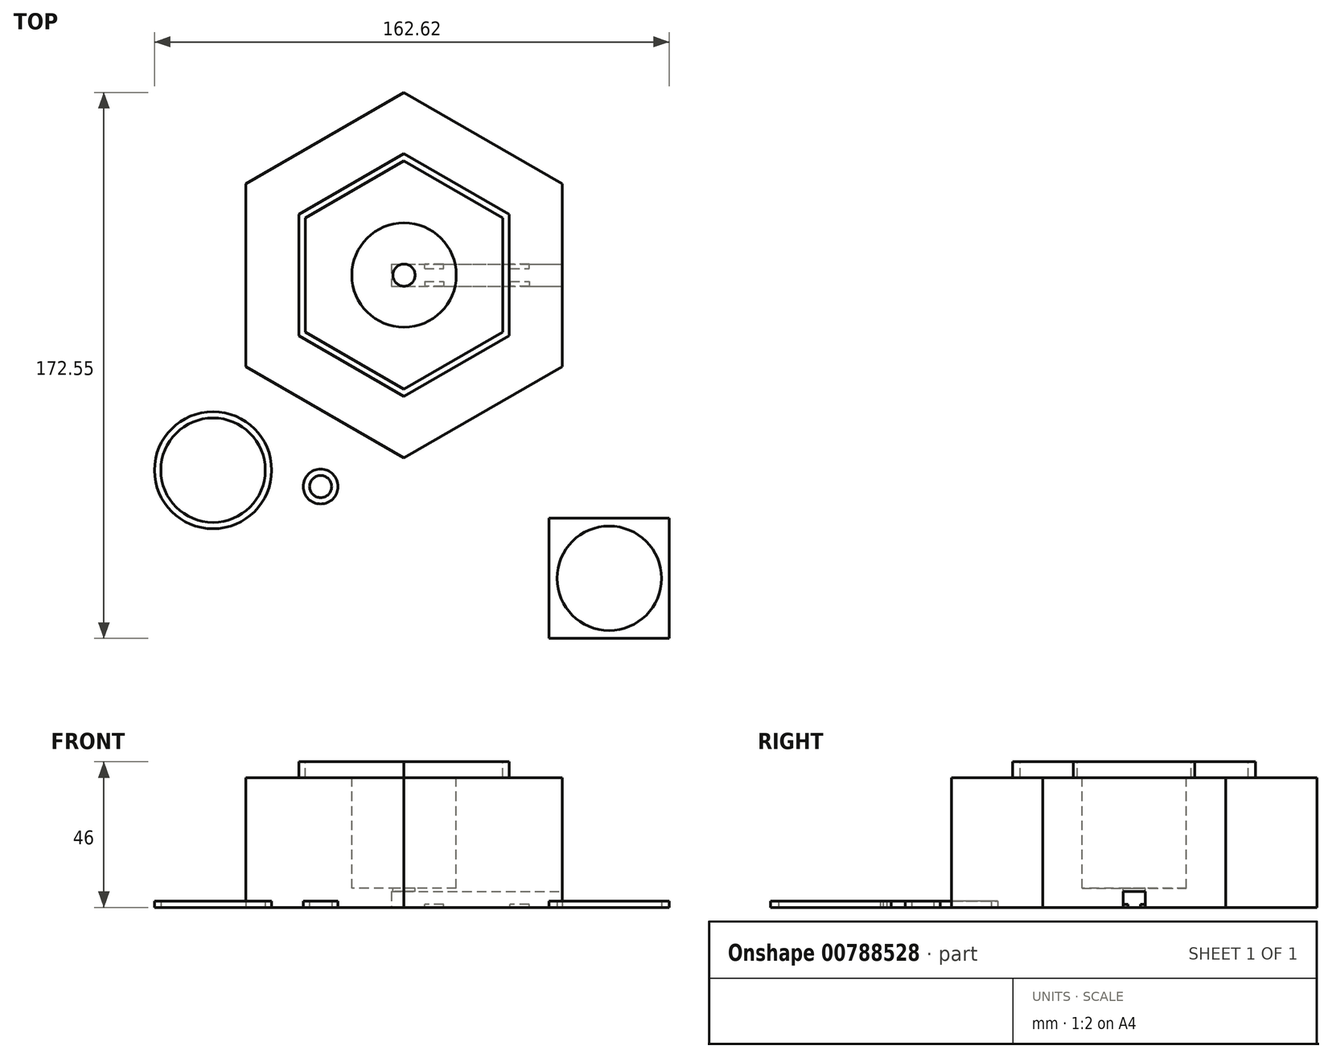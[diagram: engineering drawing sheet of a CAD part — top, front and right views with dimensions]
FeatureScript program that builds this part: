
annotation { "Feature Type Name" : "Feature", "Feature Type Description" : "" }
export const myFeature = defineFeature(function(context is Context, id is Id, definition is map)
    precondition{}
    {
        {
            var Q0;
            Q0=qCreatedBy(makeId("Top.planeOp"),FACE);
            var sketch = newSketch(context, id + "F0", { "sketchPlane" : qUnion([Q0])});
            skCircle(sketch, "E0.cCircle", {"center": v(0, 0) * mm, "radius": 50 * mm, "construction": true});
            skLineSegment(sketch, "E0.0", {"start": v(0, 57.73) * mm, "end": v(50, 28.87) * mm});
            skLineSegment(sketch, "E0.1", {"start": v(50, 28.87) * mm, "end": v(50, -28.87) * mm});
            skLineSegment(sketch, "E0.2", {"start": v(50, -28.87) * mm, "end": v(0, -57.73) * mm});
            skLineSegment(sketch, "E0.3", {"start": v(0, -57.73) * mm, "end": v(-50, -28.87) * mm});
            skLineSegment(sketch, "E0.4", {"start": v(-50, -28.87) * mm, "end": v(-50, 28.87) * mm});
            skLineSegment(sketch, "E0.5", {"start": v(-50, 28.87) * mm, "end": v(0, 57.73) * mm});
            skPoint(sketch, "E0.0.midPoint", {"position": v(25, 43.3) * mm});
            skSolve(sketch);
        }
        {
            var Q0;
            Q0 = qSketchRegion(id + "F0", true);
            extrude(context, id + "F1", {"entities" : qUnion([Q0]), "depth" : 41 * mm, "offsetDistance" : 25 * mm});
        }
        {
            var Q0;
            Q0=makeQuery(id+"F1.opExtrude","CAP_FACE",FACE,{"disambiguationData":[OSD([sQuery(id+"F0.wireOp",EDGE,"E0.0"),sQuery(id+"F0.wireOp",EDGE,"E0.1"),sQuery(id+"F0.wireOp",EDGE,"E0.2"),sQuery(id+"F0.wireOp",EDGE,"E0.3"),sQuery(id+"F0.wireOp",EDGE,"E0.4"),sQuery(id+"F0.wireOp",EDGE,"E0.5")])],"isStart":false});
            var sketch = newSketch(context, id + "F2", { "sketchPlane" : qUnion([Q0])});
            skCircle(sketch, "E1.cCircle", {"center": v(0, 0) * mm, "radius": 33.21 * mm, "construction": true});
            skLineSegment(sketch, "E1.0", {"start": v(0, 38.35) * mm, "end": v(33.21, 19.17) * mm});
            skLineSegment(sketch, "E1.1", {"start": v(33.21, 19.17) * mm, "end": v(33.21, -19.17) * mm});
            skLineSegment(sketch, "E1.2", {"start": v(33.21, -19.17) * mm, "end": v(0, -38.35) * mm});
            skLineSegment(sketch, "E1.3", {"start": v(0, -38.35) * mm, "end": v(-33.21, -19.17) * mm});
            skLineSegment(sketch, "E1.4", {"start": v(-33.21, -19.17) * mm, "end": v(-33.21, 19.17) * mm});
            skLineSegment(sketch, "E1.5", {"start": v(-33.21, 19.17) * mm, "end": v(0, 38.35) * mm});
            skPoint(sketch, "E1.0.midPoint", {"position": v(16.6, 28.76) * mm});
            skSolve(sketch);
        }
        {
            var Q0;
            Q0 = qSketchRegion(id + "F2", true);
            extrude(context, id + "F3", {"entities" : qUnion([Q0]), "operationType" : NewBodyOperationType.ADD, "depth" : 5 * mm, "offsetDistance" : 25 * mm});
        }
        {
            var Q0;
            Q0=makeQuery(id+"F3.opExtrude","CAP_FACE",FACE,{"disambiguationData":[OSD([sQuery(id+"F2.wireOp",EDGE,"E1.0"),sQuery(id+"F2.wireOp",EDGE,"E1.1"),sQuery(id+"F2.wireOp",EDGE,"E1.2"),sQuery(id+"F2.wireOp",EDGE,"E1.3"),sQuery(id+"F2.wireOp",EDGE,"E1.4"),sQuery(id+"F2.wireOp",EDGE,"E1.5")])],"isStart":false});
            var sketch = newSketch(context, id + "F4", { "sketchPlane" : qUnion([Q0])});
            skCircle(sketch, "E2.cCircle", {"center": v(0, 0) * mm, "radius": 31.21 * mm, "construction": true});
            skLineSegment(sketch, "E2.0", {"start": v(0, 36.04) * mm, "end": v(31.21, 18.02) * mm});
            skLineSegment(sketch, "E2.1", {"start": v(31.21, 18.02) * mm, "end": v(31.21, -18.02) * mm});
            skLineSegment(sketch, "E2.2", {"start": v(31.21, -18.02) * mm, "end": v(0, -36.04) * mm});
            skLineSegment(sketch, "E2.3", {"start": v(0, -36.04) * mm, "end": v(-31.21, -18.02) * mm});
            skLineSegment(sketch, "E2.4", {"start": v(-31.21, -18.02) * mm, "end": v(-31.21, 18.02) * mm});
            skLineSegment(sketch, "E2.5", {"start": v(-31.21, 18.02) * mm, "end": v(0, 36.04) * mm});
            skPoint(sketch, "E2.0.midPoint", {"position": v(15.6, 27.03) * mm});
            skSolve(sketch);
        }
        {
            var Q0;
            Q0 = qSketchRegion(id + "F4", true);
            extrude(context, id + "F5", {"entities" : qUnion([Q0]), "operationType" : NewBodyOperationType.REMOVE, "oppositeDirection" : true, "depth" : 5 * mm, "offsetDistance" : 25 * mm});
        }
        {
            var Q0;
            Q0=makeQuery(id+"F5.boolean.opBoolean","COPY",FACE,{"derivedFrom":makeQuery(id+"F5.opExtrude","CAP_FACE",FACE,{"disambiguationData":[OSD([sQuery(id+"F4.wireOp",EDGE,"E2.0"),sQuery(id+"F4.wireOp",EDGE,"E2.1"),sQuery(id+"F4.wireOp",EDGE,"E2.2"),sQuery(id+"F4.wireOp",EDGE,"E2.3"),sQuery(id+"F4.wireOp",EDGE,"E2.4"),sQuery(id+"F4.wireOp",EDGE,"E2.5")])],"isStart":false})});
            var sketch = newSketch(context, id + "F6", { "sketchPlane" : qUnion([Q0])});
            skCircle(sketch, "E3", {"center": v(0, 0) * mm, "radius": 16.5 * mm});
            skSolve(sketch);
        }
        {
            var Q0;
            Q0=makeQuery(id+"F6.imprint","IMPRINT",FACE,{"disambiguationData":[TD([[makeQuery(id+"F6.imprint","IMPRINT",EDGE,{"derivedFrom":sQuery(id+"F6.wireOp",EDGE,"E3")}),1.0]])]});
            extrude(context, id + "F7", {"entities" : qUnion([Q0]), "operationType" : NewBodyOperationType.REMOVE, "oppositeDirection" : true, "depth" : 35 * mm, "offsetDistance" : 25 * mm});
        }
        {
            var Q0;
            Q0=makeQuery(id+"F7.boolean.opBoolean","COPY",FACE,{"derivedFrom":makeQuery(id+"F7.opExtrude","CAP_FACE",FACE,{"disambiguationData":[OSD([sQuery(id+"F6.wireOp",EDGE,"E3")])],"isStart":false})});
            var sketch = newSketch(context, id + "F8", { "sketchPlane" : qUnion([Q0])});
            skSolve(sketch);
        }
        {
            var Q0;
            Q0=makeQuery(id+"F8.imprint","IMPRINT",FACE,{"disambiguationData":[TD([[makeQuery(id+"F8.imprint","IMPRINT",EDGE,{"derivedFrom":makeQuery(id+"F7.boolean.opBoolean","COPY",EDGE,{"derivedFrom":makeQuery(id+"F7.opExtrude","CAP_EDGE",EDGE,{"disambiguationData":[OSD([sQuery(id+"F6.wireOp",EDGE,"E3")])],"isStart":false})})}),1.0]])]});
            var sketch = newSketch(context, id + "F9", { "sketchPlane" : qUnion([Q0])});
            skCircle(sketch, "E4", {"center": v(0, 0) * mm, "radius": 3.5 * mm});
            skSolve(sketch);
        }
        {
            var Q0;
            Q0 = qSketchRegion(id + "F9", true);
            extrude(context, id + "F10", {"entities" : qUnion([Q0]), "operationType" : NewBodyOperationType.REMOVE, "oppositeDirection" : true, "depth" : 25 * mm, "offsetDistance" : 25 * mm});
        }
        {
            var Q0;
            Q0=makeQuery(id+"F1.opExtrude","SWEPT_FACE",FACE,{"disambiguationData":[OSD([sQuery(id+"F0.wireOp",EDGE,"E0.1")])]});
            var sketch = newSketch(context, id + "F11", { "sketchPlane" : qUnion([Q0])});
            skLineSegment(sketch, "E5.top", {"start": v(3.5, 5) * mm, "end": v(-3.5, 5) * mm});
            skPoint(sketch, "E5.middle", {"position": v(0, 0) * mm});
            skLineSegment(sketch, "E6.top", {"start": v(-3.5, 0) * mm, "end": v(3.5, 0) * mm});
            skLineSegment(sketch, "E6.left", {"start": v(-3.5, 5) * mm, "end": v(-3.5, 0) * mm});
            skLineSegment(sketch, "E6.right", {"start": v(3.5, 5) * mm, "end": v(3.5, 0) * mm});
            skSolve(sketch);
        }
        {
            var Q0;
            {var subQ0=sQuery(id+"F11.wireOp",EDGE,"E5.top");Q0=makeQuery(id+"F11.imprint","IMPRINT",FACE,{"disambiguationData":[TD([[makeQuery(id+"F11.imprint","IMPRINT",EDGE,{"derivedFrom":subQ0}),1.0]])]});}
            extrude(context, id + "F12", {"entities" : qUnion([Q0]), "operationType" : NewBodyOperationType.REMOVE, "oppositeDirection" : true, "depth" : 54 * mm, "offsetDistance" : 25 * mm});
        }
        {
            var Q0;
            Q0=makeQuery(id+"F12.boolean.opBoolean","COPY",FACE,{"derivedFrom":makeQuery(id+"F12.opExtrude","SWEPT_FACE",FACE,{"disambiguationData":[OSD([sQuery(id+"F11.wireOp",EDGE,"E6.left")])]})});
            var sketch = newSketch(context, id + "F13", { "sketchPlane" : qUnion([Q0])});
            skPoint(sketch, "E7", {"position": v(-23, 0) * mm});
            skPoint(sketch, "E8", {"position": v(4, 0) * mm});
            skPoint(sketch, "E9", {"position": v(-50, 0) * mm});
            skPoint(sketch, "E10", {"position": v(-9.5, 0) * mm});
            skLineSegment(sketch, "E11.bottom", {"start": v(-12.5, 0) * mm, "end": v(-6.5, 0) * mm});
            skLineSegment(sketch, "E11.top", {"start": v(-12.5, 1) * mm, "end": v(-6.5, 1) * mm});
            skLineSegment(sketch, "E11.left", {"start": v(-12.5, 0) * mm, "end": v(-12.5, 1) * mm});
            skLineSegment(sketch, "E11.right", {"start": v(-6.5, 0) * mm, "end": v(-6.5, 1) * mm});
            skPoint(sketch, "E12", {"position": v(-36.5, 0) * mm});
            skLineSegment(sketch, "E13.bottom", {"start": v(-39.5, 0) * mm, "end": v(-33.5, 0) * mm});
            skLineSegment(sketch, "E13.top", {"start": v(-39.5, 1) * mm, "end": v(-33.5, 1) * mm});
            skLineSegment(sketch, "E13.left", {"start": v(-39.5, 0) * mm, "end": v(-39.5, 1) * mm});
            skLineSegment(sketch, "E13.right", {"start": v(-33.5, 0) * mm, "end": v(-33.5, 1) * mm});
            skSolve(sketch);
        }
        {
            var Q0;
            Q0 = qSketchRegion(id + "F13", true);
            extrude(context, id + "F14", {"entities" : qUnion([Q0]), "operationType" : NewBodyOperationType.ADD, "depth" : 1.5 * mm, "offsetDistance" : 25 * mm});
        }
        {
            var Q0;
            Q0=makeQuery(id+"F12.boolean.opBoolean","COPY",FACE,{"derivedFrom":makeQuery(id+"F12.opExtrude","SWEPT_FACE",FACE,{"disambiguationData":[OSD([sQuery(id+"F11.wireOp",EDGE,"E6.right")])]})});
            var sketch = newSketch(context, id + "F15", { "sketchPlane" : qUnion([Q0])});
            skPoint(sketch, "E14", {"position": v(50, 0) * mm});
            skPoint(sketch, "E15", {"position": v(-4, 0) * mm});
            skPoint(sketch, "E16", {"position": v(23, 0) * mm});
            skPoint(sketch, "E17", {"position": v(36.5, 0) * mm});
            skPoint(sketch, "E18", {"position": v(9.5, 0) * mm});
            skLineSegment(sketch, "E19.bottom", {"start": v(39.5, 0) * mm, "end": v(33.5, 0) * mm});
            skLineSegment(sketch, "E19.top", {"start": v(39.5, 1) * mm, "end": v(33.5, 1) * mm});
            skLineSegment(sketch, "E19.left", {"start": v(39.5, 0) * mm, "end": v(39.5, 1) * mm});
            skLineSegment(sketch, "E19.right", {"start": v(33.5, 0) * mm, "end": v(33.5, 1) * mm});
            skLineSegment(sketch, "E20.bottom", {"start": v(12.5, 0) * mm, "end": v(6.5, 0) * mm});
            skLineSegment(sketch, "E20.top", {"start": v(12.5, 1) * mm, "end": v(6.5, 1) * mm});
            skLineSegment(sketch, "E20.left", {"start": v(12.5, 0) * mm, "end": v(12.5, 1) * mm});
            skLineSegment(sketch, "E20.right", {"start": v(6.5, 0) * mm, "end": v(6.5, 1) * mm});
            skSolve(sketch);
        }
        {
            var Q0;
            Q0 = qSketchRegion(id + "F15", true);
            extrude(context, id + "F16", {"entities" : qUnion([Q0]), "operationType" : NewBodyOperationType.ADD, "depth" : 1.5 * mm, "offsetDistance" : 25 * mm});
        }
        {
            var Q0;
            Q0=qCreatedBy(makeId("Top.planeOp"),FACE);
            var sketch = newSketch(context, id + "F17", { "sketchPlane" : qUnion([Q0])});
            skCircle(sketch, "E21", {"center": v(-60.31, -61.65) * mm, "radius": 16.5 * mm});
            skCircle(sketch, "E22", {"center": v(-60.31, -61.65) * mm, "radius": 18.5 * mm});
            skSolve(sketch);
        }
        {
            var Q0;
            Q0 = qSketchRegion(id + "F17", true);
            extrude(context, id + "F18", {"entities" : qUnion([Q0]), "depth" : 2 * mm, "offsetDistance" : 25 * mm});
        }
        {
            var Q0;
            Q0=qCreatedBy(makeId("Top.planeOp"),FACE);
            var sketch = newSketch(context, id + "F19", { "sketchPlane" : qUnion([Q0])});
            skCircle(sketch, "E23", {"center": v(-26.34, -66.83) * mm, "radius": 3.5 * mm});
            skCircle(sketch, "E24", {"center": v(-26.34, -66.83) * mm, "radius": 5.5 * mm});
            skSolve(sketch);
        }
        {
            var Q0;
            Q0 = qSketchRegion(id + "F19", true);
            extrude(context, id + "F20", {"entities" : qUnion([Q0]), "depth" : 2 * mm, "offsetDistance" : 25 * mm});
        }
        {
            var Q0;
            Q0=qCreatedBy(makeId("Top.planeOp"),FACE);
            var sketch = newSketch(context, id + "F21", { "sketchPlane" : qUnion([Q0])});
            skCircle(sketch, "E25", {"center": v(64.81, -95.82) * mm, "radius": 16.5 * mm});
            skLineSegment(sketch, "E26.bottom", {"start": v(83.81, -114.82) * mm, "end": v(45.81, -114.82) * mm});
            skLineSegment(sketch, "E26.top", {"start": v(83.81, -76.82) * mm, "end": v(45.81, -76.82) * mm});
            skLineSegment(sketch, "E26.left", {"start": v(83.81, -114.82) * mm, "end": v(83.81, -76.82) * mm});
            skLineSegment(sketch, "E26.right", {"start": v(45.81, -114.82) * mm, "end": v(45.81, -76.82) * mm});
            skSolve(sketch);
        }
        {
            var Q0;
            Q0 = qSketchRegion(id + "F21", true);
            extrude(context, id + "F22", {"entities" : qUnion([Q0]), "depth" : 2 * mm, "offsetDistance" : 25 * mm});
        }
    });
